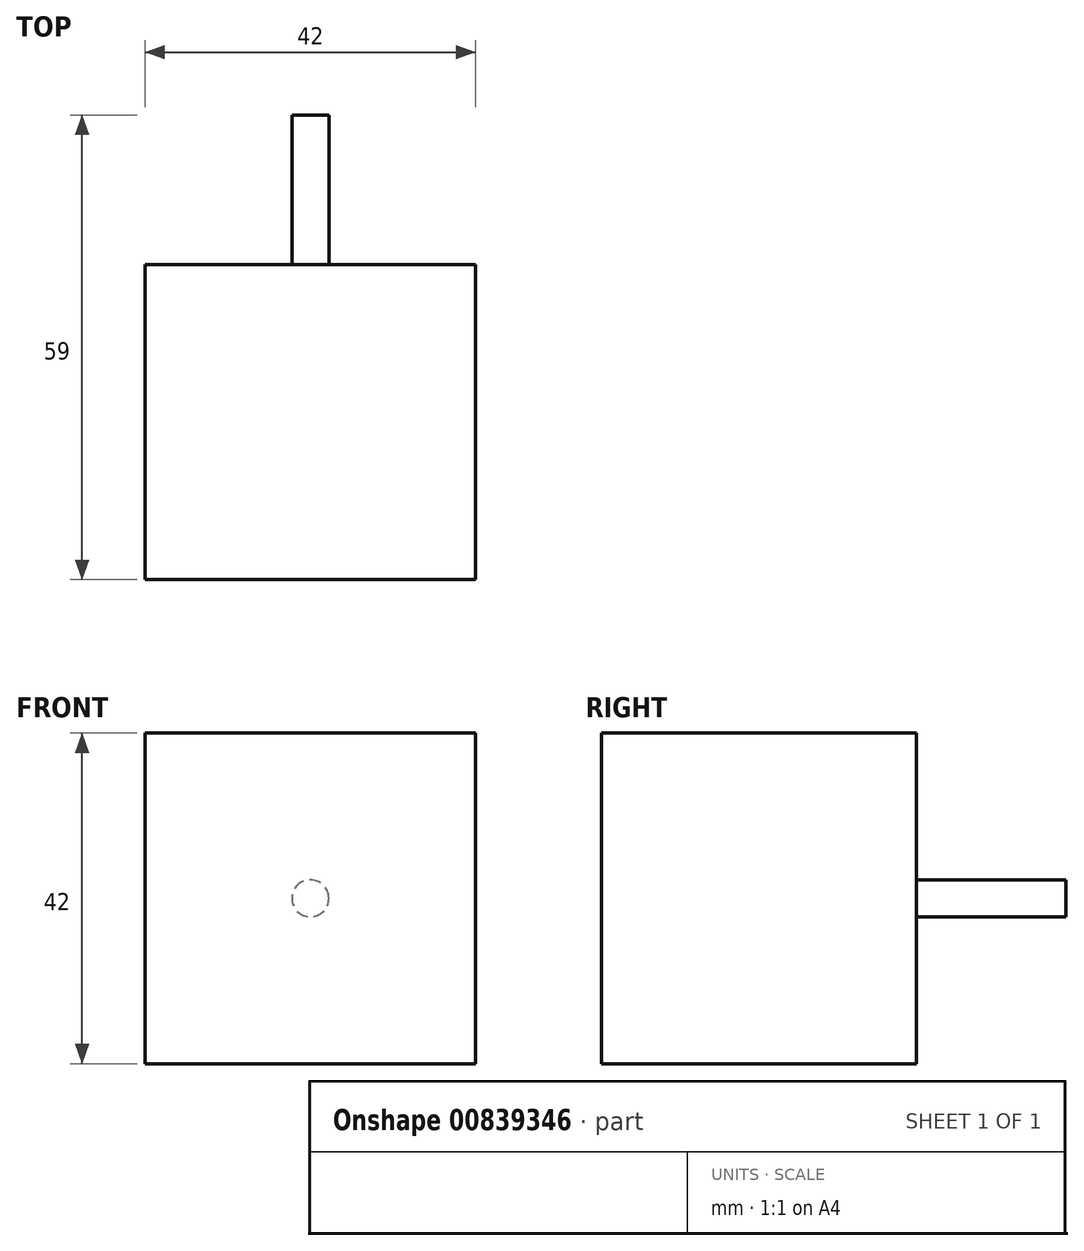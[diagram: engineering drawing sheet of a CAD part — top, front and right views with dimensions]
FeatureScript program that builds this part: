
annotation { "Feature Type Name" : "Feature", "Feature Type Description" : "" }
export const myFeature = defineFeature(function(context is Context, id is Id, definition is map)
    precondition{}
    {
        {
            var Q0;
            Q0=qCreatedBy(makeId("Front.planeOp"),FACE);
            var sketch = newSketch(context, id + "F0", { "sketchPlane" : qUnion([Q0])});
            skLineSegment(sketch, "E0", {"start": v(0, 33.45) * mm, "end": v(0, -44.25) * mm, "construction": true});
            skLineSegment(sketch, "E1", {"start": v(-42.45, 0) * mm, "end": v(44.06, 0) * mm, "construction": true});
            skLineSegment(sketch, "E2", {"start": v(-21, 0) * mm, "end": v(-21, 21) * mm});
            skLineSegment(sketch, "E3", {"start": v(-21, 21) * mm, "end": v(0, 21) * mm});
            skLineSegment(sketch, "E4.MirrorCS", {"start": v(21, 21) * mm, "end": v(0, 21) * mm});
            skLineSegment(sketch, "E5.MirrorCS", {"start": v(21, 0) * mm, "end": v(21, 21) * mm});
            skLineSegment(sketch, "E6.MirrorCS", {"start": v(-21, 0) * mm, "end": v(-21, -21) * mm});
            skLineSegment(sketch, "E7.MirrorCS", {"start": v(-21, -21) * mm, "end": v(0, -21) * mm});
            skLineSegment(sketch, "E8.MirrorCS", {"start": v(21, -21) * mm, "end": v(0, -21) * mm});
            skLineSegment(sketch, "E9.MirrorCS", {"start": v(21, 0) * mm, "end": v(21, -21) * mm});
            skSolve(sketch);
        }
        {
            var Q0;
            Q0 = qSketchRegion(id + "F0", true);
            extrude(context, id + "F1", {"entities" : qUnion([Q0]), "depth" : 40 * mm, "offsetDistance" : 25 * mm});
        }
        {
            var Q0;
            Q0=makeQuery(id+"F1.opExtrude","CAP_FACE",FACE,{"disambiguationData":[OSD([sQuery(id+"F0.wireOp",EDGE,"E2"),sQuery(id+"F0.wireOp",EDGE,"E3"),sQuery(id+"F0.wireOp",EDGE,"E4.MirrorCS"),sQuery(id+"F0.wireOp",EDGE,"E5.MirrorCS"),sQuery(id+"F0.wireOp",EDGE,"E6.MirrorCS"),sQuery(id+"F0.wireOp",EDGE,"E7.MirrorCS"),sQuery(id+"F0.wireOp",EDGE,"E8.MirrorCS"),sQuery(id+"F0.wireOp",EDGE,"E9.MirrorCS")])],"isStart":true});
            var sketch = newSketch(context, id + "F2", { "sketchPlane" : qUnion([Q0])});
            skCircle(sketch, "E10", {"center": v(0, 0) * mm, "radius": 2.35 * mm});
            skSolve(sketch);
        }
        {
            var Q0;
            Q0 = qSketchRegion(id + "F2", true);
            extrude(context, id + "F3", {"entities" : qUnion([Q0]), "operationType" : NewBodyOperationType.ADD, "depth" : 19 * mm, "offsetDistance" : 25 * mm});
        }
    });
